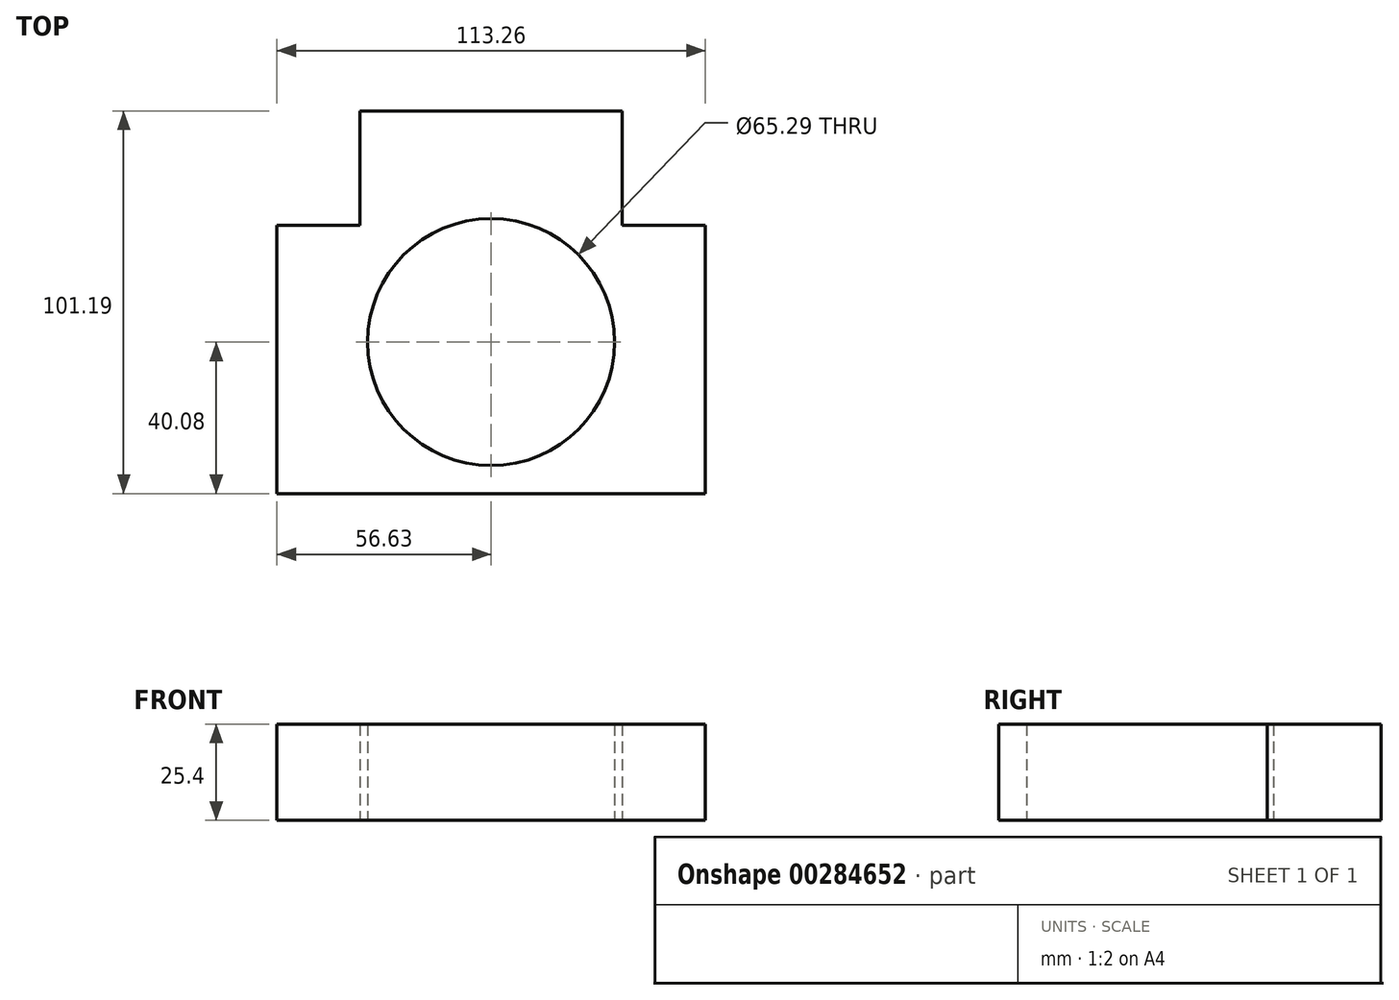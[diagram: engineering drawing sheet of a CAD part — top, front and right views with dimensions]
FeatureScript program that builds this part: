
annotation { "Feature Type Name" : "Feature", "Feature Type Description" : "" }
export const myFeature = defineFeature(function(context is Context, id is Id, definition is map)
    precondition{}
    {
        {
            var Q0;
            Q0=qCreatedBy(makeId("Top.planeOp"),FACE);
            var sketch = newSketch(context, id + "F0", { "sketchPlane" : qUnion([Q0])});
            skLineSegment(sketch, "E0", {"start": v(-56.63, 30.94) * mm, "end": v(-56.63, -40.08) * mm});
            skLineSegment(sketch, "E1", {"start": v(-56.63, -40.08) * mm, "end": v(0, -40.08) * mm});
            skLineSegment(sketch, "E2", {"start": v(-34.68, 30.94) * mm, "end": v(-34.68, 61.11) * mm});
            skLineSegment(sketch, "E3", {"start": v(-34.68, 61.11) * mm, "end": v(0, 61.11) * mm});
            skPoint(sketch, "E4.center.orphan", {"position": v(0, -4.72) * mm});
            skLineSegment(sketch, "E5.trimOffspring", {"start": v(-34.68, 30.94) * mm, "end": v(-56.63, 30.94) * mm});
            skArc(sketch, "E6", {"start": v(0, 32.65) * mm, "mid": v(-32.65, 0) * mm, "end": v(0, -32.65) * mm});
            skPoint(sketch, "E7.end.orphan", {"position": v(56.76, 30.94) * mm});
            skLineSegment(sketch, "E8.trimOffspring", {"start": v(0, 0) * mm, "end": v(0, -4.72) * mm});
            skPoint(sketch, "E9.start.orphan", {"position": v(0, 68.73) * mm});
            skLineSegment(sketch, "E10.MirrorCS", {"start": v(56.63, -40.08) * mm, "end": v(0, -40.08) * mm});
            skLineSegment(sketch, "E11.MirrorCS", {"start": v(34.68, 61.11) * mm, "end": v(0, 61.11) * mm});
            skArc(sketch, "E12.MirrorCS", {"start": v(0, 32.65) * mm, "mid": v(32.65, 0) * mm, "end": v(0, -32.65) * mm});
            skLineSegment(sketch, "E13.MirrorCS", {"start": v(34.68, 30.94) * mm, "end": v(56.63, 30.94) * mm});
            skLineSegment(sketch, "E14.MirrorCS", {"start": v(34.68, 30.94) * mm, "end": v(34.68, 61.11) * mm});
            skLineSegment(sketch, "E15.MirrorCS", {"start": v(56.63, 30.94) * mm, "end": v(56.63, -40.08) * mm});
            skSolve(sketch);
        }
        {
            var Q0;
            {var subQ0=sQuery(id+"F0.wireOp",EDGE,"E2");Q0=makeQuery(id+"F0.imprint","IMPRINT",FACE,{"disambiguationData":[TD([[makeQuery(id+"F0.imprint","IMPRINT",EDGE,{"derivedFrom":subQ0}),-1.0]])]});}
            var Q1;
            {var subQ3=sQuery(id+"F0.wireOp",EDGE,"E0");Q1=makeQuery(id+"F0.imprint","IMPRINT",FACE,{"disambiguationData":[TD([[makeQuery(id+"F0.imprint","IMPRINT",EDGE,{"derivedFrom":subQ3}),1.0]])]});}
            extrude(context, id + "F1", {"entities" : qUnion([Q0, Q1]), "depth" : 25.4 * mm});
        }
        {
            var Q0;
            Q0 = qSketchRegion(id + "F0", true);
            extrude(context, id + "F2", {"entities" : qUnion([Q0]), "operationType" : NewBodyOperationType.ADD, "depth" : 25.4 * mm});
        }
    });
